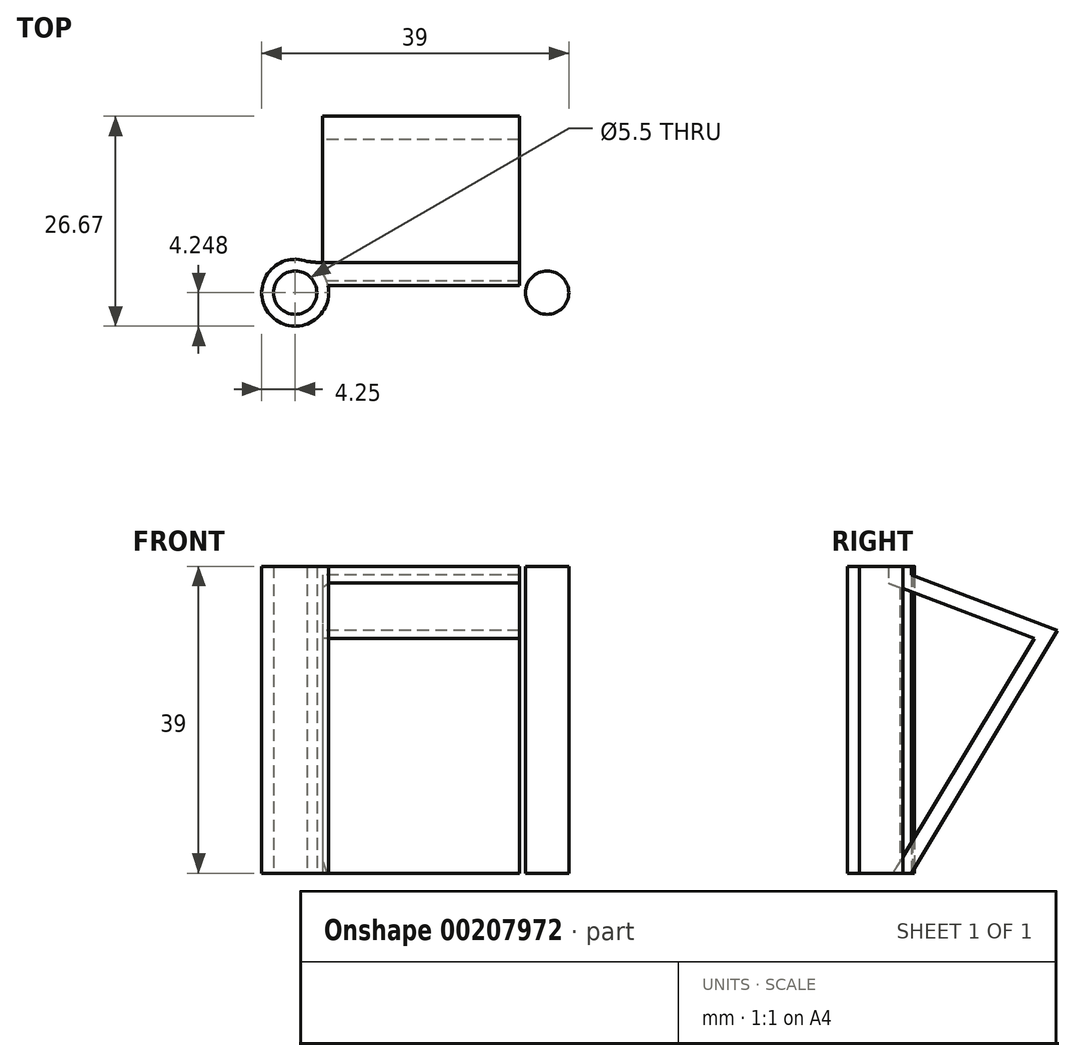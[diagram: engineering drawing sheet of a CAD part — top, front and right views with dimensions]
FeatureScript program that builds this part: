
annotation { "Feature Type Name" : "Feature", "Feature Type Description" : "" }
export const myFeature = defineFeature(function(context is Context, id is Id, definition is map)
    precondition{}
    {
        {
            var Q0;
            Q0=qCreatedBy(makeId("Right.planeOp"),FACE);
            var sketch = newSketch(context, id + "F0", { "sketchPlane" : qUnion([Q0])});
            skLineSegment(sketch, "E0.bottom", {"start": v(0, 0) * mm, "end": v(30.18, 0) * mm});
            skLineSegment(sketch, "E0.top", {"start": v(0, 39) * mm, "end": v(30.18, 39) * mm});
            skLineSegment(sketch, "E0.left", {"start": v(0, 0) * mm, "end": v(0, 39) * mm});
            skLineSegment(sketch, "E0.right", {"start": v(30.18, 0) * mm, "end": v(30.18, 39) * mm});
            skLineSegment(sketch, "E1", {"start": v(0, 39) * mm, "end": v(21.5, 30.83) * mm});
            skLineSegment(sketch, "E2", {"start": v(21.5, 30.83) * mm, "end": v(2.91, 0) * mm});
            skLineSegment(sketch, "E3.1", {"start": v(-0.71, 37.13) * mm, "end": v(18.55, 29.81) * mm});
            skLineSegment(sketch, "E4", {"start": v(18.55, 29.81) * mm, "end": v(0.58, 0) * mm});
            skSolve(sketch);
        }
        {
            var Q0;
            {var subQ3=sQuery(id+"F0.wireOp",EDGE,"E1");Q0=makeQuery(id+"F0.imprint","IMPRINT",FACE,{"disambiguationData":[TD([[makeQuery(id+"F0.imprint","IMPRINT",EDGE,{"derivedFrom":subQ3}),-1.0]])]});}
            extrude(context, id + "F1", {"entities" : qUnion([Q0]), "depth" : 25 * mm});
        }
        {
            var Q0;
            Q0=makeQuery(id+"F1.opExtrude","SWEPT_FACE",FACE,{"disambiguationData":[OSD([sQuery(id+"F0.wireOp",EDGE,"E0.bottom")])]});
            var sketch = newSketch(context, id + "F2", { "sketchPlane" : qUnion([Q0])});
            skLineSegment(sketch, "E5", {"start": v(12.5, -0.58) * mm, "end": v(12.5, 3.82) * mm, "construction": true});
            skLineSegment(sketch, "E6", {"start": v(12.5, 0.92) * mm, "end": v(-3.5, 0.92) * mm, "construction": true});
            skCircle(sketch, "E7", {"center": v(-3.5, 0.92) * mm, "radius": 2.75 * mm});
            skCircle(sketch, "E8", {"center": v(-3.5, 0.92) * mm, "radius": 4.25 * mm});
            skCircle(sketch, "E9.MirrorC", {"center": v(28.5, 0.92) * mm, "radius": 4.25 * mm});
            skCircle(sketch, "E10.MirrorC", {"center": v(28.5, 0.92) * mm, "radius": 2.75 * mm});
            skSolve(sketch);
        }
        {
            var Q0;
            Q0=makeQuery(id+"F2.imprint","IMPRINT",FACE,{"disambiguationData":[TD([[makeQuery(id+"F2.imprint","IMPRINT",EDGE,{"derivedFrom":sQuery(id+"F2.wireOp",EDGE,"E7")}),-1.0]])]});
            var Q1;
            {var subQ0=sQuery(id+"F2.wireOp",EDGE,"E8");var subQ1=sQuery(id+"F0.wireOp",EDGE,"E0.bottom");var subQ4=makeQuery(id+"F1.opExtrude","CAP_EDGE",EDGE,{"disambiguationData":[OSD([subQ1])],"isStart":true});var subQ5=makeQuery(id+"F2.imprint","INTERSECT",VERTEX,{"derivedFrom":[subQ4,subQ0]});Q1=makeQuery(id+"F2.imprint","IMPRINT",FACE,{"disambiguationData":[TD([[makeQuery(id+"F2.imprint","IMPRINT",EDGE,{"disambiguationData":[TD([[subQ5,-1.0]])],"derivedFrom":subQ0}),1.0]])]});}
            var Q2;
            Q2=makeQuery(id+"F2.imprint","IMPRINT",FACE,{"disambiguationData":[TD([[makeQuery(id+"F2.imprint","IMPRINT",EDGE,{"derivedFrom":sQuery(id+"F2.wireOp",EDGE,"E10.MirrorC")}),1.0]])]});
            var Q3;
            {var subQ0=sQuery(id+"F2.wireOp",EDGE,"E9.MirrorC");var subQ1=sQuery(id+"F0.wireOp",EDGE,"E0.bottom");var subQ4=makeQuery(id+"F1.opExtrude","CAP_EDGE",EDGE,{"disambiguationData":[OSD([subQ1])],"isStart":false});var subQ5=makeQuery(id+"F2.imprint","INTERSECT",VERTEX,{"derivedFrom":[subQ4,subQ0]});Q3=makeQuery(id+"F2.imprint","IMPRINT",FACE,{"disambiguationData":[TD([[makeQuery(id+"F2.imprint","IMPRINT",EDGE,{"disambiguationData":[TD([[subQ5,-1.0]])],"derivedFrom":subQ0}),-1.0]])]});}
            extrude(context, id + "F3", {"entities" : qUnion([Q0, Q1, Q2, Q3]), "operationType" : NewBodyOperationType.ADD, "oppositeDirection" : true, "depth" : 39 * mm});
        }
        {
            var Q0;
            Q0=makeQuery(id+"F1.opExtrude","SWEPT_FACE",FACE,{"disambiguationData":[OSD([sQuery(id+"F0.wireOp",EDGE,"E1")])]});
            var sketch = newSketch(context, id + "F4", { "sketchPlane" : qUnion([Q0])});
            skLineSegment(sketch, "E11", {"start": v(0, -12.26) * mm, "end": v(25, -12.26) * mm});
            skSolve(sketch);
        }
        {
            var Q0;
            Q0=makeQuery(id+"F3.boolean.opBoolean","MERGE",FACE,{"derivedFrom":[makeQuery(id+"F1.opExtrude","SWEPT_FACE",FACE,{"disambiguationData":[OSD([sQuery(id+"F0.wireOp",EDGE,"E0.bottom")])]}),makeQuery(id+"F3.opExtrude","CAP_FACE",FACE,{"disambiguationData":[OSD([sQuery(id+"F2.wireOp",EDGE,"E7"),sQuery(id+"F2.wireOp",EDGE,"E8")])],"isStart":true}),makeQuery(id+"F3.opExtrude","CAP_FACE",FACE,{"disambiguationData":[OSD([sQuery(id+"F2.wireOp",EDGE,"E9.MirrorC"),sQuery(id+"F2.wireOp",EDGE,"E10.MirrorC")])],"isStart":true})]});
            var sketch = newSketch(context, id + "F5", { "sketchPlane" : qUnion([Q0])});
            skArc(sketch, "E12", {"start": v(0, -2.91) * mm, "mid": v(-1.71, -3.02) * mm, "end": v(-3.4, -3.33) * mm});
            skLineSegment(sketch, "E13", {"start": v(12.5, -0.58) * mm, "end": v(12.5, -2.91) * mm, "construction": true});
            skArc(sketch, "E14.MirrorCS", {"start": v(25, -2.91) * mm, "mid": v(26.71, -3.02) * mm, "end": v(28.4, -3.33) * mm});
            skSolve(sketch);
        }
        {
            var Q0;
            {var subQ1=sQuery(id+"F0.wireOp",EDGE,"E0.bottom");var subQ2=makeQuery(id+"F1.opExtrude","CAP_EDGE",EDGE,{"disambiguationData":[OSD([subQ1])],"isStart":true});Q0=makeQuery(id+"F5.imprint","IMPRINT",FACE,{"disambiguationData":[TD([[makeQuery(id+"F5.imprint","IMPRINT",EDGE,{"derivedFrom":subQ2}),-1.0]])]});}
            var Q1;
            {var subQ1=sQuery(id+"F0.wireOp",EDGE,"E0.bottom");var subQ2=makeQuery(id+"F1.opExtrude","CAP_EDGE",EDGE,{"disambiguationData":[OSD([subQ1])],"isStart":false});Q1=makeQuery(id+"F5.imprint","IMPRINT",FACE,{"disambiguationData":[TD([[makeQuery(id+"F5.imprint","IMPRINT",EDGE,{"derivedFrom":subQ2}),1.0]])]});}
            var Q2;
            Q2=makeQuery(id+"F3.opExtrude","CAP_FACE",FACE,{"disambiguationData":[OSD([sQuery(id+"F2.wireOp",EDGE,"E7"),sQuery(id+"F2.wireOp",EDGE,"E8")])],"isStart":false});
            extrude(context, id + "F6", {"entities" : qUnion([Q0, Q1]), "operationType" : NewBodyOperationType.ADD, "endBound" : BoundingType.UP_TO_SURFACE, "oppositeDirection" : true, "endBoundEntityFace" : qUnion([Q2]), "depth" : 25 * mm});
        }
        {
            var Q0;
            {var subQ2=sQuery(id+"F0.wireOp",EDGE,"E1");var subQ3=sQuery(id+"F0.wireOp",EDGE,"E0.bottom");Q0=makeQuery(id+"F6.boolean.opBoolean","SPLIT",FACE,{"disambiguationData":[TD([makeQuery(id+"F1.opExtrude","SWEPT_FACE",FACE,{"disambiguationData":[OSD([subQ2])]})])],"derivedFrom":makeQuery(id+"F6.opExtrude","SWEPT_FACE",FACE,{"disambiguationData":[OSD([subQ3]),TDD([makeQuery(id+"F5.imprint","IMPRINT",EDGE,{"derivedFrom":makeQuery(id+"F1.opExtrude","CAP_EDGE",EDGE,{"disambiguationData":[OSD([subQ3])],"isStart":true})})])]})});}
            extrude(context, id + "F7", {"entities" : qUnion([Q0]), "operationType" : NewBodyOperationType.ADD, "depth" : 25 * mm});
        }
        {
            var Q0;
            Q0=makeQuery(id+"F7.opExtrude","SWEPT_FACE",FACE,{"disambiguationData":[OSD([sQuery(id+"F0.wireOp",EDGE,"E0.bottom"),sQuery(id+"F2.wireOp",EDGE,"E8")])]});
            var Q1;
            Q1=makeQuery(id+"F1.opExtrude","SWEPT_FACE",FACE,{"disambiguationData":[OSD([sQuery(id+"F0.wireOp",EDGE,"E0.left")])]});
            extrude(context, id + "F8", {"entities" : qUnion([Q0]), "operationType" : NewBodyOperationType.ADD, "endBound" : BoundingType.UP_TO_SURFACE, "endBoundEntityFace" : qUnion([Q1]), "depth" : 25 * mm});
        }
    });
